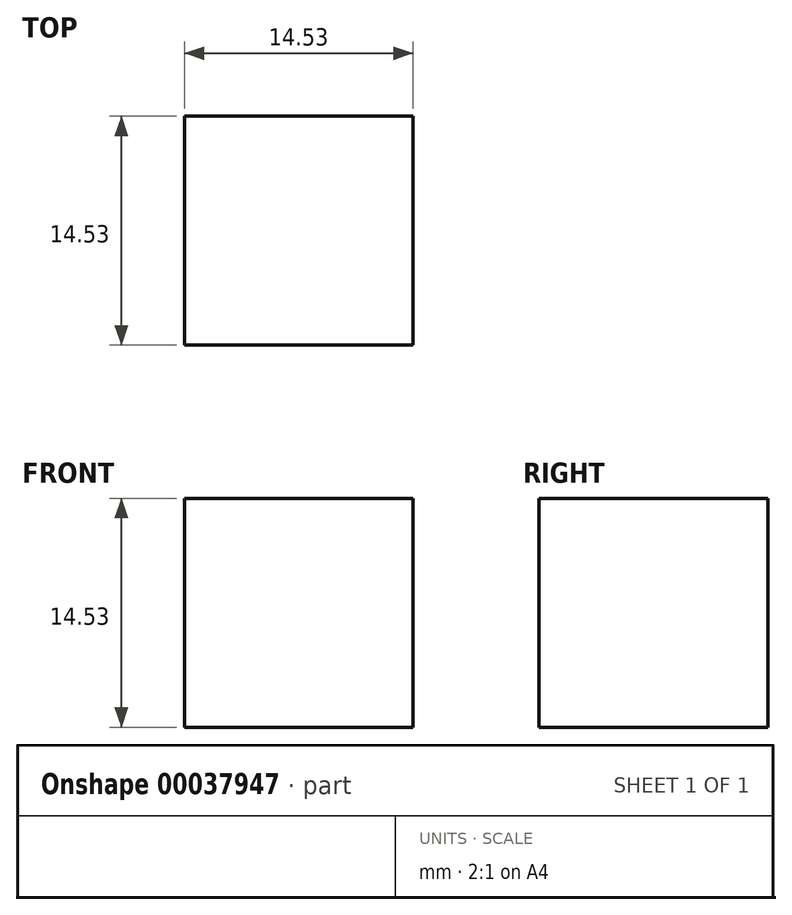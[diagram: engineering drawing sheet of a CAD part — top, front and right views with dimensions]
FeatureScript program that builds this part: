
annotation { "Feature Type Name" : "Feature", "Feature Type Description" : "" }
export const myFeature = defineFeature(function(context is Context, id is Id, definition is map)
    precondition{}
    {
        {
            var Q0;
            Q0=qCreatedBy(makeId("Top.planeOp"),FACE);
            var sketch = newSketch(context, id + "F0", { "sketchPlane" : qUnion([Q0])});
            skLineSegment(sketch, "E0.bottom", {"start": v(0, 0) * mm, "end": v(14.53, 0) * mm});
            skLineSegment(sketch, "E0.top", {"start": v(0, -14.53) * mm, "end": v(14.53, -14.53) * mm});
            skLineSegment(sketch, "E0.left", {"start": v(0, 0) * mm, "end": v(0, -14.53) * mm});
            skLineSegment(sketch, "E0.right", {"start": v(14.53, 0) * mm, "end": v(14.53, -14.53) * mm});
            skSolve(sketch);
        }
        {
            var Q0;
            Q0 = qSketchRegion(id + "F0", true);
            extrude(context, id + "F1", {"entities" : qUnion([Q0]), "depth" : 14.53 * mm});
        }
    });
